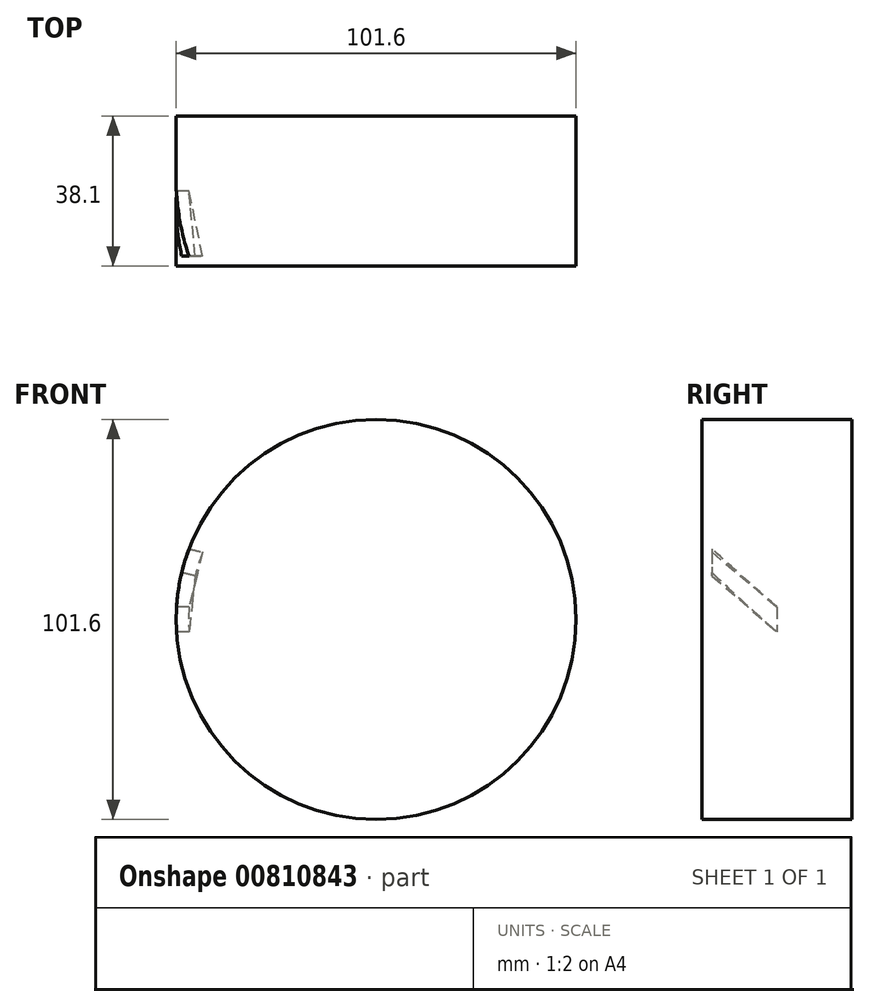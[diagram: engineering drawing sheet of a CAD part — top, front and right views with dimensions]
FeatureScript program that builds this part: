
annotation { "Feature Type Name" : "Feature", "Feature Type Description" : "" }
export const myFeature = defineFeature(function(context is Context, id is Id, definition is map)
    precondition{}
    {
        {
            var Q0;
            Q0=qCreatedBy(makeId("Front.planeOp"),FACE);
            var sketch = newSketch(context, id + "F0", { "sketchPlane" : qUnion([Q0])});
            skCircle(sketch, "E0", {"center": v(0, 0) * mm, "radius": 50.8 * mm});
            skSolve(sketch);
        }
        {
            var Q0;
            Q0=makeQuery(id+"F0.imprint","IMPRINT",FACE,{"disambiguationData":[TD([[makeQuery(id+"F0.imprint","IMPRINT",EDGE,{"derivedFrom":sQuery(id+"F0.wireOp",EDGE,"E0")}),1.0]])]});
            extrude(context, id + "F1", {"entities" : qUnion([Q0]), "depth" : 38.1 * mm, "offsetDistance" : 25.4 * mm});
        }
        {
            var Q0;
            Q0=makeQuery(id+"F1.opExtrude","CAP_FACE",FACE,{"disambiguationData":[OSD([sQuery(id+"F0.wireOp",EDGE,"E0")])],"isStart":false});
            cPlane(context, id + "F2", {"entities" : qUnion([Q0]), "cplaneType" : CPlaneType.OFFSET, "offset" : 19.05 * mm, "oppositeDirection" : true, "width" : 152.4 * mm, "height" : 152.4 * mm});
        }
        {
            var Q0;
            Q0=makeQuery(id+"F1.opExtrude","CAP_FACE",FACE,{"disambiguationData":[OSD([sQuery(id+"F0.wireOp",EDGE,"E0")])],"isStart":false});
            var sketch = newSketch(context, id + "F3", { "sketchPlane" : qUnion([Q0])});
            skLineSegment(sketch, "E1", {"start": v(0, 0) * mm, "end": v(-53.7, 19.55) * mm, "construction": true});
            skLineSegment(sketch, "E2", {"start": v(0, 0) * mm, "end": v(-50.8, 0) * mm, "construction": true});
            skLineSegment(sketch, "E3.0", {"start": v(-43.57, 19.24) * mm, "end": v(-52.62, 22.53) * mm});
            skArc(sketch, "E4", {"start": v(-43.57, 19.24) * mm, "mid": v(-44.75, 16.29) * mm, "end": v(-45.74, 13.27) * mm});
            skLineSegment(sketch, "E5", {"start": v(-52.62, 22.53) * mm, "end": v(-54.79, 16.56) * mm});
            skLineSegment(sketch, "E6.trimOffspring", {"start": v(-45.74, 13.27) * mm, "end": v(-54.79, 16.56) * mm});
            skSolve(sketch);
        }
        {
            var Q0;
            Q0=qCreatedBy(id+"F2.planeOp",FACE);
            var sketch = newSketch(context, id + "F4", { "sketchPlane" : qUnion([Q0])});
            skLineSegment(sketch, "E7", {"start": v(0, 0) * mm, "end": v(-57.15, 0) * mm, "construction": true});
            skArc(sketch, "E8", {"start": v(-47.52, 3.18) * mm, "mid": v(-47.63, 0) * mm, "end": v(-47.52, -3.17) * mm});
            skLineSegment(sketch, "E9.0", {"start": v(-47.52, 3.17) * mm, "end": v(-57.15, 3.17) * mm});
            skLineSegment(sketch, "E10.0", {"start": v(-47.52, -3.18) * mm, "end": v(-57.15, -3.18) * mm});
            skLineSegment(sketch, "E11", {"start": v(-57.15, 3.17) * mm, "end": v(-57.15, -3.18) * mm});
            skSolve(sketch);
        }
        {
            var Q1;
            {var subQ0=sQuery(id+"F3.wireOp",EDGE,"E4");Q1=makeQuery(id+"F3.imprint","IMPRINT",FACE,{"disambiguationData":[TD([[makeQuery(id+"F3.imprint","IMPRINT",EDGE,{"derivedFrom":subQ0}),-1.0]])]});}
            var Q2;
            Q2=makeQuery(id+"F4.imprint","IMPRINT",FACE,{"disambiguationData":[TD([[makeQuery(id+"F4.imprint","IMPRINT",EDGE,{"derivedFrom":sQuery(id+"F4.wireOp",EDGE,"E8")}),-1.0]])]});
            loft(context, id + "F5", {"operationType" : NewBodyOperationType.REMOVE, "sheetProfilesArray" : [{ "sheetProfileEntities" : qUnion([Q1]) }, { "sheetProfileEntities" : qUnion([Q2]) }]});
        }
        {
            var Q0;
            Q0=makeQuery(id+"F1.opExtrude","CAP_FACE",FACE,{"disambiguationData":[OSD([sQuery(id+"F0.wireOp",EDGE,"E0")])],"isStart":false});
            var sketch = newSketch(context, id + "F6", { "sketchPlane" : qUnion([Q0])});
            skCircle(sketch, "E12", {"center": v(0, 0) * mm, "radius": 50.8 * mm});
            skSolve(sketch);
        }
        {
            var Q0;
            Q0 = qSketchRegion(id + "F6", true);
            extrude(context, id + "F7", {"entities" : qUnion([Q0]), "operationType" : NewBodyOperationType.ADD, "oppositeDirection" : true, "depth" : 2.54 * mm, "offsetDistance" : 25.4 * mm});
        }
    });
